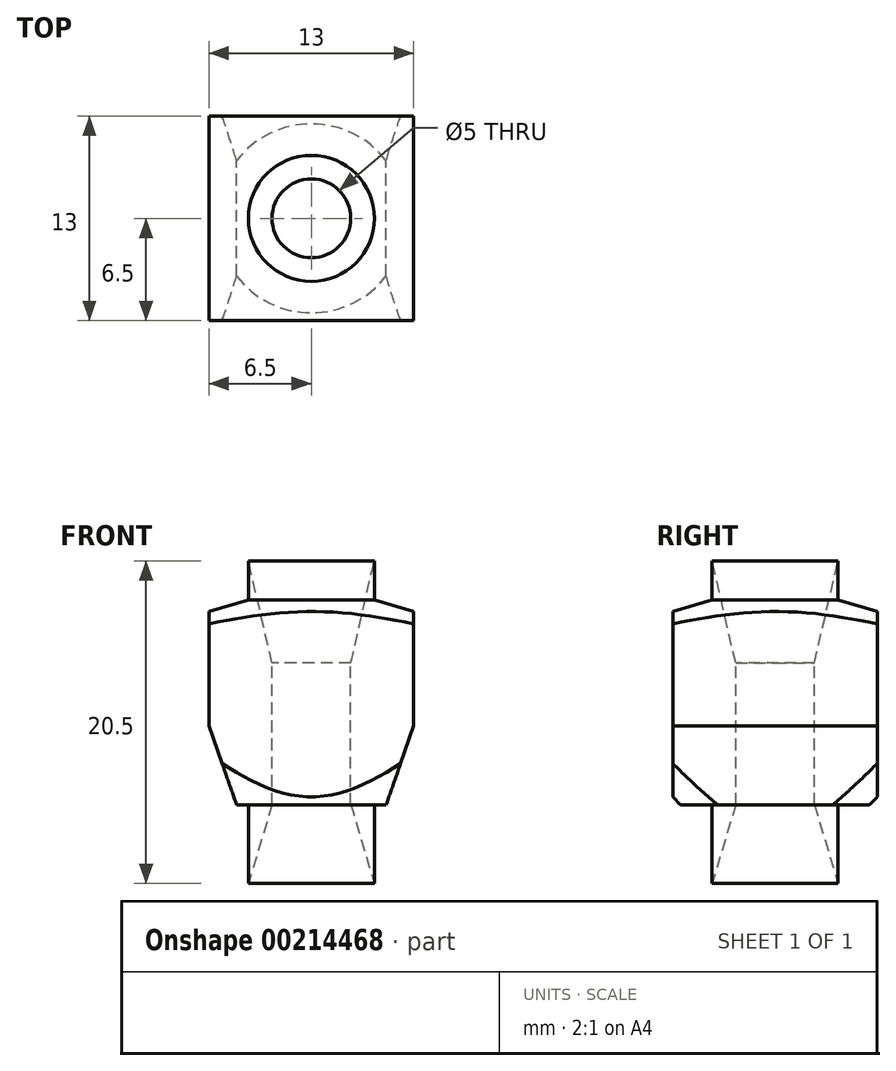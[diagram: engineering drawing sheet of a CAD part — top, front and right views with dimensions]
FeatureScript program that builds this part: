
annotation { "Feature Type Name" : "Feature", "Feature Type Description" : "" }
export const myFeature = defineFeature(function(context is Context, id is Id, definition is map)
    precondition{}
    {
        {
            var Q0;
            Q0=qCreatedBy(makeId("Front.planeOp"),FACE);
            var sketch = newSketch(context, id + "F0", { "sketchPlane" : qUnion([Q0])});
            skLineSegment(sketch, "E0", {"start": v(0, 9.66) * mm, "end": v(0, -9.44) * mm, "construction": true});
            skLineSegment(sketch, "E1", {"start": v(4, 0) * mm, "end": v(4, -2.5) * mm});
            skLineSegment(sketch, "E2", {"start": v(4, -2.5) * mm, "end": v(15.64, -5.86) * mm});
            skLineSegment(sketch, "E3", {"start": v(4, -15.5) * mm, "end": v(4, -15.5) * mm});
            skLineSegment(sketch, "E4", {"start": v(4, -15.5) * mm, "end": v(4, -20.5) * mm});
            skLineSegment(sketch, "E5", {"start": v(4, -20.5) * mm, "end": v(2.5, -15.5) * mm});
            skLineSegment(sketch, "E6", {"start": v(2.5, -15.5) * mm, "end": v(2.5, -6.5) * mm});
            skLineSegment(sketch, "E7", {"start": v(2.5, -6.5) * mm, "end": v(4, 0) * mm});
            skLineSegment(sketch, "E8", {"start": v(4, -15.5) * mm, "end": v(6, -15.5) * mm});
            skLineSegment(sketch, "E9", {"start": v(6, -15.5) * mm, "end": v(15.64, -5.86) * mm});
            skSolve(sketch);
        }
        {
            var Q0;
            Q0 = qSketchRegion(id + "F0", true);
            var Q1;
            Q1=sQuery(id+"F0.wireOp",EDGE,"E0");
            revolve(context, id + "F1", {"entities" : qUnion([Q0]), "axis" : qUnion([Q1]), "revolveType" : RevolveType.FULL});
        }
        {
            var Q0;
            Q0=qCreatedBy(makeId("Front.planeOp"),FACE);
            var sketch = newSketch(context, id + "F2", { "sketchPlane" : qUnion([Q0])});
            skLineSegment(sketch, "E10", {"start": v(4, 0) * mm, "end": v(6.5, 0) * mm});
            skLineSegment(sketch, "E11", {"start": v(6.5, 0) * mm, "end": v(6.5, -10.5) * mm});
            skLineSegment(sketch, "E12", {"start": v(6.5, -10.5) * mm, "end": v(4.75, -15.5) * mm});
            skLineSegment(sketch, "E13", {"start": v(4.75, -15.5) * mm, "end": v(4.75, -20.5) * mm});
            skLineSegment(sketch, "E14", {"start": v(4.75, -20.5) * mm, "end": v(0, -20.5) * mm});
            skLineSegment(sketch, "E15", {"start": v(0, 2.53) * mm, "end": v(0, -26.47) * mm, "construction": true});
            skLineSegment(sketch, "E16.MirrorCS", {"start": v(-6.5, 0) * mm, "end": v(-6.5, -10.5) * mm});
            skLineSegment(sketch, "E17.MirrorCS", {"start": v(-4.75, -20.5) * mm, "end": v(0, -20.5) * mm});
            skLineSegment(sketch, "E18.MirrorCS", {"start": v(-4, 0) * mm, "end": v(-6.5, 0) * mm});
            skLineSegment(sketch, "E19.MirrorCS", {"start": v(4, 0) * mm, "end": v(-4, 0) * mm});
            skLineSegment(sketch, "E20.MirrorCS", {"start": v(-4.75, -15.5) * mm, "end": v(-4.75, -20.5) * mm});
            skLineSegment(sketch, "E21.MirrorCS", {"start": v(-6.5, -10.5) * mm, "end": v(-4.75, -15.5) * mm});
            skSolve(sketch);
        }
        {
            var Q0;
            Q0 = qSketchRegion(id + "F2", true);
            extrude(context, id + "F3", {"entities" : qUnion([Q0]), "operationType" : NewBodyOperationType.INTERSECT, "endBound" : BoundingType.SYMMETRIC, "depth" : 13 * mm});
        }
    });
